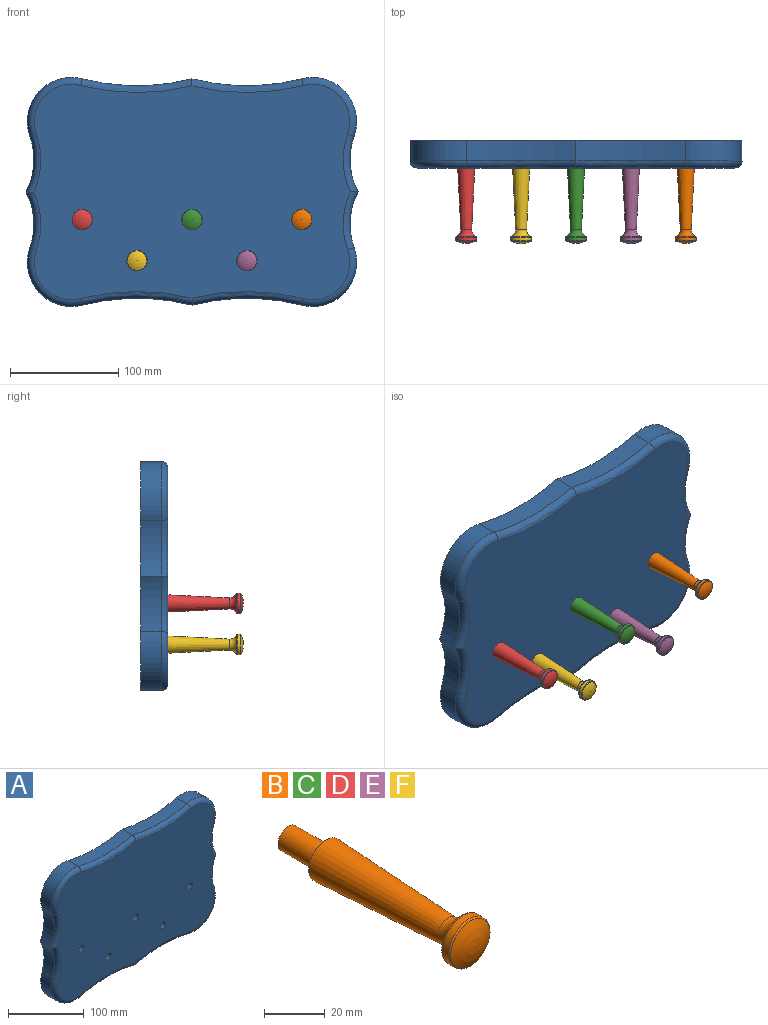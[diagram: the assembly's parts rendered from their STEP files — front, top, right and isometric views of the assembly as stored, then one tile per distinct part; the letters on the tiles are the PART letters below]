
ASSEMBLY  parts=6 mates=5
PART A: 36 faces, bbox 311.5x25.4x218.8 mm
  f0: cylinder r=64.52mm len=51.57mm, axis (0,-1,0), area 1013.2mm2, adj f1,f3,f5,f17
  f1: cylinder r=40.8mm len=54.48mm, axis (0,-1,0), area 1681.1mm2, adj f0,f2,f3,f15
  f2: cylinder r=205mm len=101.5mm, axis (0,-1,0), area 1953.9mm2, adj f1,f3,f10,f14
  f3: plane 307.34x212.09mm, normal (0,1,0), area 60044.5mm2, adj f0,f1,f2,f5,f6,f7,f8,f9
  f4: plane 293.18x199.39mm, normal (0,-1,0), area 53492.1mm2, adj f14,f15,f16,f17,f18,f19,f20,f21
  f5: cylinder r=64.52mm len=51.57mm, axis (0,-1,0), area 1013.2mm2, adj f0,f3,f6,f19
  f6: cylinder r=40.8mm len=54.48mm, axis (0,-1,0), area 1681.1mm2, adj f3,f5,f7,f21
  f7: cylinder r=205mm len=101.5mm, axis (0,-1,0), area 1953.9mm2, adj f3,f6,f13,f23
  f8: cylinder r=64.52mm len=51.57mm, axis (0,-1,0), area 1013.2mm2, adj f3,f9,f11,f20
  f9: cylinder r=40.8mm len=54.48mm, axis (0,-1,0), area 1681.1mm2, adj f3,f8,f10,f18
  f10: cylinder r=205mm len=101.5mm, axis (0,-1,0), area 1953.9mm2, adj f2,f3,f9,f16
  f11: cylinder r=64.52mm len=51.57mm, axis (0,-1,0), area 1013.2mm2, adj f3,f8,f12,f22
  f12: cylinder r=40.8mm len=54.48mm, axis (0,-1,0), area 1681.1mm2, adj f3,f11,f13,f24
  f13: cylinder r=205mm len=101.5mm, axis (0,-1,0), area 1953.9mm2, adj f3,f7,f12,f25
  f14: torus R=211.35mm, axis (0,-1,0), area 1028.7mm2, adj f2,f4,f15,f16
  f15: torus R=34.45mm, axis (0,-1,0), area 830.4mm2, adj f1,f4,f14,f17
  f16: torus R=211.35mm, axis (0,-1,0), area 1028.7mm2, adj f4,f10,f14,f18
  f17: torus R=70.87mm, axis (0,-1,0), area 537.5mm2, adj f0,f4,f15,f19
  f18: torus R=34.45mm, axis (0,-1,0), area 830.4mm2, adj f4,f9,f16,f20
  f19: torus R=70.87mm, axis (0,-1,0), area 537.5mm2, adj f4,f5,f17,f21
  f20: torus R=70.87mm, axis (0,-1,0), area 537.5mm2, adj f4,f8,f18,f22
  f21: torus R=34.45mm, axis (0,-1,0), area 830.4mm2, adj f4,f6,f19,f23
  f22: torus R=70.87mm, axis (0,-1,0), area 537.5mm2, adj f4,f11,f20,f24
  f23: torus R=211.35mm, axis (0,-1,0), area 1028.7mm2, adj f4,f7,f21,f25
  f24: torus R=34.45mm, axis (0,-1,0), area 830.4mm2, adj f4,f12,f22,f25
  f25: torus R=211.35mm, axis (0,-1,0), area 1028.7mm2, adj f4,f13,f23,f24
  f26: cylinder r=5.56mm len=19.05mm, axis (0,-1,0), area 665.1mm2, adj f4,f27
  f27: plane 11.11x11.11mm, normal (0,-1,0), area 97mm2, adj f26
  f28: cylinder r=5.56mm len=19.05mm, axis (0,-1,0), area 665.1mm2, adj f4,f29
  f29: plane 11.11x11.11mm, normal (0,-1,0), area 97mm2, adj f28
  f30: cylinder r=5.56mm len=19.05mm, axis (0,-1,0), area 665.1mm2, adj f4,f31
  f31: plane 11.11x11.11mm, normal (0,-1,0), area 97mm2, adj f30
  f32: cylinder r=5.56mm len=19.05mm, axis (0,-1,0), area 665.1mm2, adj f4,f33
  f33: plane 11.11x11.11mm, normal (0,-1,0), area 97mm2, adj f32
  f34: cylinder r=5.56mm len=19.05mm, axis (0,-1,0), area 665.1mm2, adj f4,f35
  f35: plane 11.11x11.11mm, normal (0,-1,0), area 97mm2, adj f34
PART B: 9 faces, bbox 24.7x87.4x24.7 mm
  f0: cylinder r=4.76mm len=17.53mm, axis (0,-1,0), area 524.4mm2, adj f1,f2
  f1: plane 9.53x9.53mm, normal (0,1,0), area 71.3mm2, adj f0
  f2: plane 15.88x15.88mm, normal (0,1,0), area 126.7mm2, adj f0,f3
  f3: cone r=7.94mm half-angle=2.9deg, axis (0,1,0), area 2339.3mm2, adj f2,f6
  f4: cylinder r=9.53mm len=19.05mm, axis (0,-1,0), area 168.5mm2, adj f7,f8
  f5: sphere r=19.05mm, area 278.8mm2, adj f8
  f6: torus R=11.42mm, axis (0,-1,0), area 316.3mm2, adj f3,f7
  f7: torus R=8.76mm, axis (0,1,0), area 53.2mm2, adj f4,f6
  f8: torus R=8.76mm, axis (0,1,0), area 48.1mm2, adj f4,f5
PART C: same geometry as B
PART D: same geometry as B
PART E: same geometry as B
PART F: same geometry as B
PLACE A rot(axis=(0.84,-0.46,0.28),0deg) t=(12.92,-75.16,130.92)mm
PLACE B rot(axis=(0.84,-0.46,0.28),0deg) t=(114.52,-75.16,105.52)mm
PLACE C rot(axis=(0.84,-0.46,0.28),0deg) t=(12.92,-75.16,105.52)mm
PLACE D rot(axis=(0.84,-0.46,0.28),0deg) t=(-88.68,-75.16,105.52)mm
PLACE E rot(axis=(0.84,-0.46,0.28),0deg) t=(63.72,-75.16,67.42)mm
PLACE F rot(axis=(0.84,-0.46,0.28),0deg) t=(-37.88,-75.16,67.42)mm
MATE fastened B.f0 <-> A.f34  axis (0,1,0) through (114.52,-75.16,105.52)mm
MATE fastened C.f0 <-> A.f26  axis (0,1,0) through (12.92,-75.16,105.52)mm
MATE fastened D.f0 <-> A.f30  axis (0,1,0) through (-88.68,-75.16,105.52)mm
MATE fastened E.f0 <-> A.f32  axis (0,1,0) through (63.72,-75.16,67.42)mm
MATE fastened F.f0 <-> A.f28  axis (0,1,0) through (-37.88,-75.16,67.42)mm
